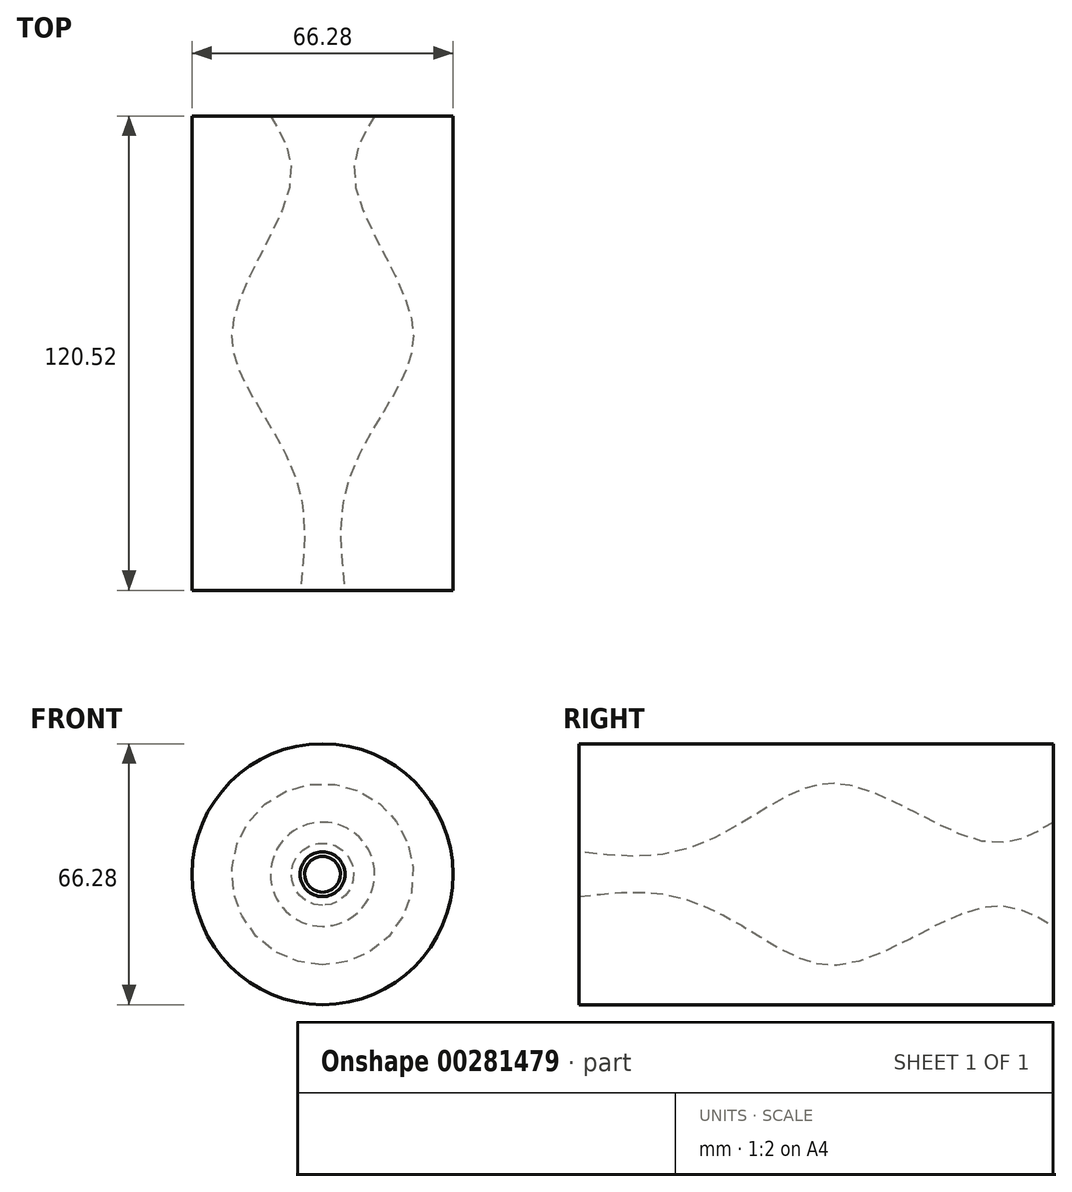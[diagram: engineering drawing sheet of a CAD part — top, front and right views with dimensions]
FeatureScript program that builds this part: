
annotation { "Feature Type Name" : "Feature", "Feature Type Description" : "" }
export const myFeature = defineFeature(function(context is Context, id is Id, definition is map)
    precondition{}
    {
        {
            var Q0;
            Q0=qCreatedBy(makeId("Right.planeOp"),FACE);
            var sketch = newSketch(context, id + "F0", { "sketchPlane" : qUnion([Q0])});
            skLineSegment(sketch, "E0", {"start": v(-58.75, 5.7) * mm, "end": v(-58.75, 33.14) * mm});
            skLineSegment(sketch, "E1", {"start": v(-58.75, 33.14) * mm, "end": v(61.77, 33.14) * mm});
            skLineSegment(sketch, "E2", {"start": v(61.77, 33.14) * mm, "end": v(61.77, 13.22) * mm});
            skFitSpline(sketch, "E3", {"points": [v(-58.75, 5.7) * mm, v(-34.65, 5.52) * mm, v(-12.39, 16.07) * mm, v(9.2, 22.76) * mm, v(44.52, 8.2) * mm, v(61.77, 13.22) * mm], "startDerivative": vector(125.18, -14.5) * mm, "endDerivative": vector(90.8, 55.23) * mm});
            skPoint(sketch, "E4.orphan", {"position": v(-58.75, 0) * mm});
            skPoint(sketch, "E5.orphan", {"position": v(61.77, 0) * mm});
            skSolve(sketch);
        }
        {
            var Q0;
            Q0=qCreatedBy(makeId("Right.planeOp"),FACE);
            var sketch = newSketch(context, id + "F1", { "sketchPlane" : qUnion([Q0])});
            skLineSegment(sketch, "E6", {"start": v(-81.52, 0) * mm, "end": v(91.56, 0) * mm});
            skSolve(sketch);
        }
        {
            var Q0;
            Q0=makeQuery(id+"F0.imprint","IMPRINT",FACE,{"disambiguationData":[TD([[makeQuery(id+"F0.imprint","IMPRINT",EDGE,{"derivedFrom":sQuery(id+"F0.wireOp",EDGE,"E0")}),-1.0]])]});
            var Q1;
            Q1=sQuery(id+"F1.wireOp",EDGE,"E6");
            revolve(context, id + "F2", {"entities" : qUnion([Q0]), "axis" : qUnion([Q1]), "revolveType" : RevolveType.FULL});
        }
    });
